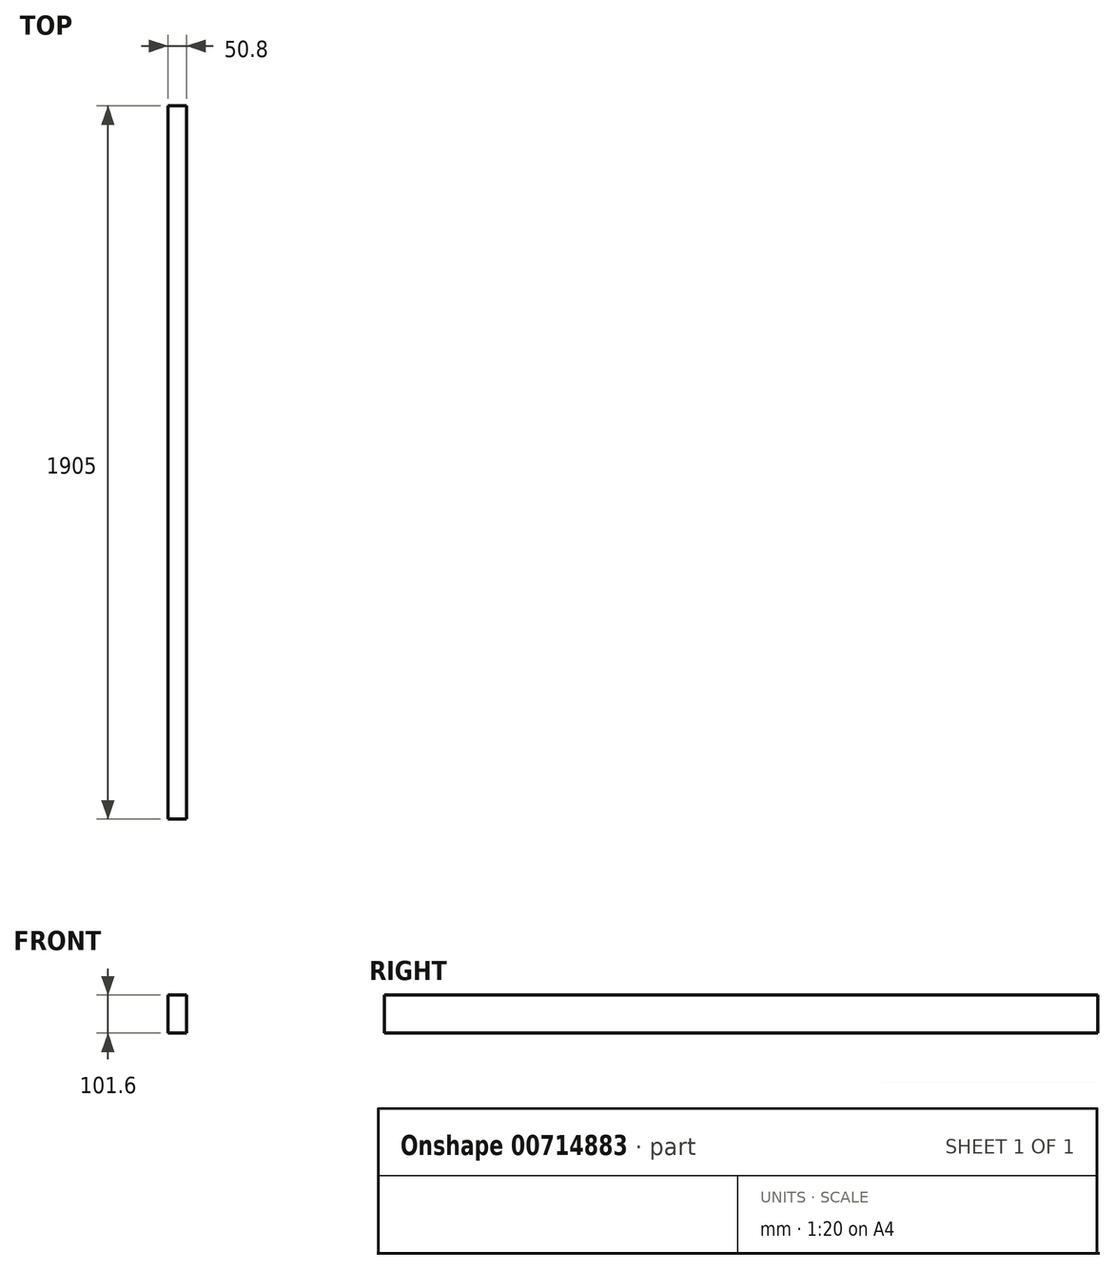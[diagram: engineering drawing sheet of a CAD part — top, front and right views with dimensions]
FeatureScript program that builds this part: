
annotation { "Feature Type Name" : "Feature", "Feature Type Description" : "" }
export const myFeature = defineFeature(function(context is Context, id is Id, definition is map)
    precondition{}
    {
        {
            var Q0;
            Q0=qCreatedBy(makeId("Right.planeOp"),FACE);
            var sketch = newSketch(context, id + "F0", { "sketchPlane" : qUnion([Q0])});
            skLineSegment(sketch, "E0.bottom", {"start": v(1905, 101.6) * mm, "end": v(0, 101.6) * mm});
            skLineSegment(sketch, "E0.top", {"start": v(1905, 0) * mm, "end": v(0, 0) * mm});
            skLineSegment(sketch, "E0.left", {"start": v(1905, 101.6) * mm, "end": v(1905, 0) * mm});
            skLineSegment(sketch, "E0.right", {"start": v(0, 101.6) * mm, "end": v(0, 0) * mm});
            skSolve(sketch);
        }
        {
            var Q0;
            Q0=makeQuery(id+"F0.imprint","IMPRINT",FACE,{"disambiguationData":[TD([[makeQuery(id+"F0.imprint","IMPRINT",EDGE,{"derivedFrom":sQuery(id+"F0.wireOp",EDGE,"E0.bottom")}),1.0]])]});
            extrude(context, id + "F1", {"entities" : qUnion([Q0]), "depth" : 50.8 * mm, "offsetDistance" : 25.4 * mm});
        }
    });
